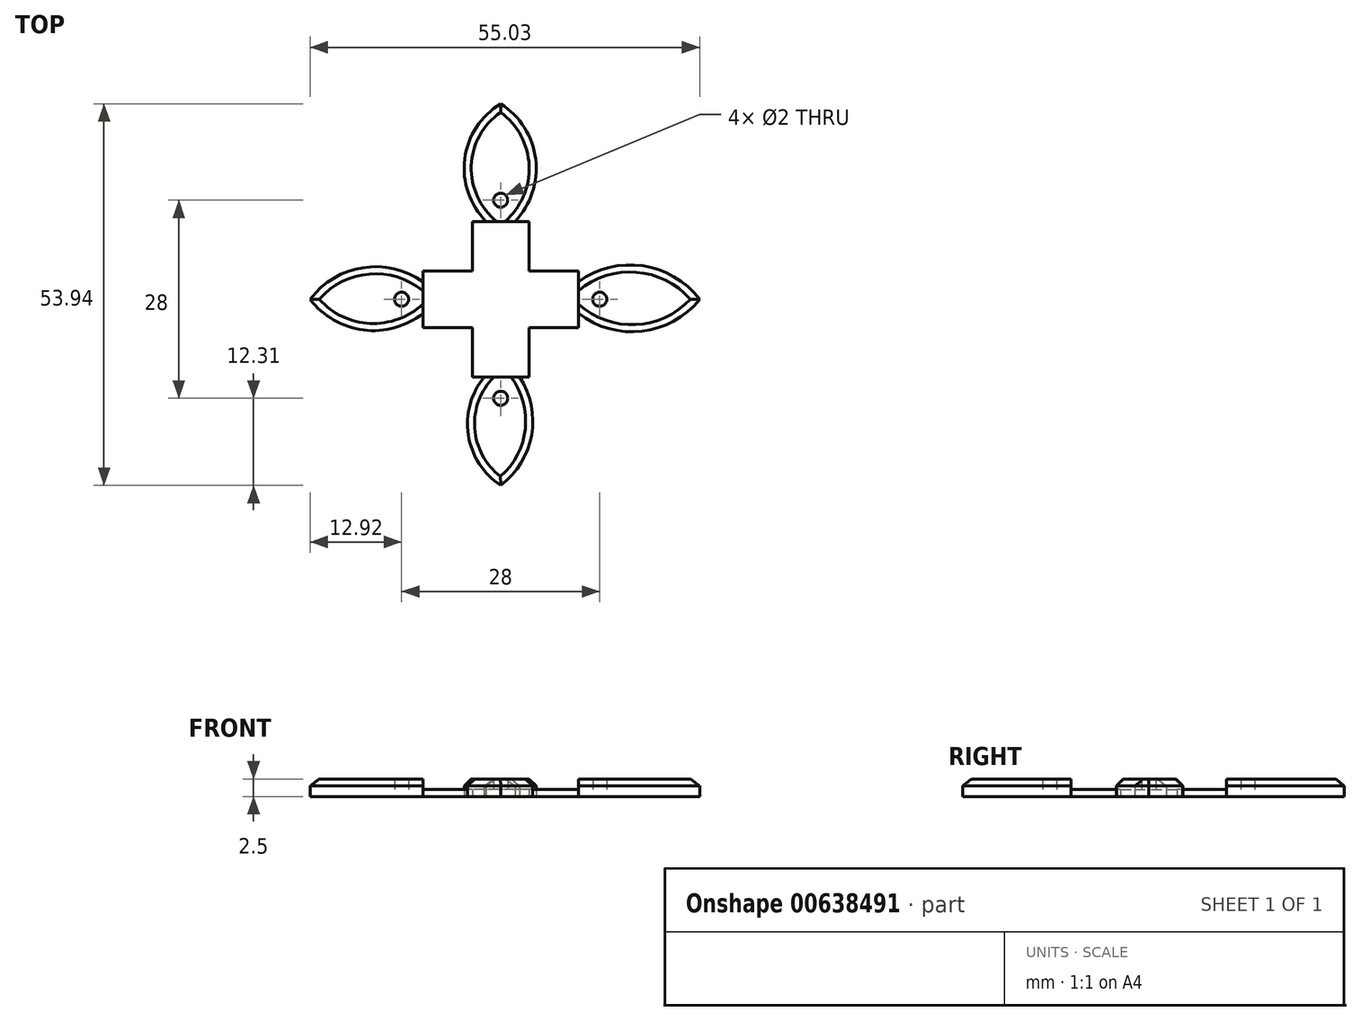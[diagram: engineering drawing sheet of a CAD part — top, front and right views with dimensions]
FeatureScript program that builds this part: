
annotation { "Feature Type Name" : "Feature", "Feature Type Description" : "" }
export const myFeature = defineFeature(function(context is Context, id is Id, definition is map)
    precondition{}
    {
        {
            var Q0;
            Q0=qCreatedBy(makeId("Top.planeOp"),FACE);
            var sketch = newSketch(context, id + "F0", { "sketchPlane" : qUnion([Q0])});
            skLineSegment(sketch, "E0.bottom", {"start": v(11, -4) * mm, "end": v(-11, -4) * mm});
            skLineSegment(sketch, "E0.top", {"start": v(11, 4) * mm, "end": v(-11, 4) * mm});
            skLineSegment(sketch, "E0.left", {"start": v(11, -4) * mm, "end": v(11, 4) * mm});
            skLineSegment(sketch, "E0.right", {"start": v(-11, -4) * mm, "end": v(-11, 4) * mm});
            skPoint(sketch, "E0.middle", {"position": v(0, 0) * mm});
            skLineSegment(sketch, "E1.bottom", {"start": v(4, 11) * mm, "end": v(-4, 11) * mm});
            skLineSegment(sketch, "E1.top", {"start": v(4, -11) * mm, "end": v(-4, -11) * mm});
            skLineSegment(sketch, "E1.left", {"start": v(4, 11) * mm, "end": v(4, -11) * mm});
            skLineSegment(sketch, "E1.right", {"start": v(-4, 11) * mm, "end": v(-4, -11) * mm});
            skSolve(sketch);
        }
        {
            var Q0;
            {var subQ0=sQuery(id+"F0.wireOp",EDGE,"E1.left");var subQ1=sQuery(id+"F0.wireOp",EDGE,"E0.bottom");var subQ2=makeQuery(id+"F0.imprint","INTERSECT",VERTEX,{"derivedFrom":[subQ1,subQ0]});Q0=makeQuery(id+"F0.imprint","IMPRINT",FACE,{"disambiguationData":[TD([[makeQuery(id+"F0.imprint","IMPRINT",EDGE,{"disambiguationData":[TD([[subQ2,-1.0]])],"derivedFrom":subQ1}),-1.0]])]});}
            var Q1;
            {var subQ0=sQuery(id+"F0.wireOp",EDGE,"E0.right");Q1=makeQuery(id+"F0.imprint","IMPRINT",FACE,{"disambiguationData":[TD([[makeQuery(id+"F0.imprint","IMPRINT",EDGE,{"derivedFrom":subQ0}),-1.0]])]});}
            var Q2;
            {var subQ5=sQuery(id+"F0.wireOp",EDGE,"E1.bottom");Q2=makeQuery(id+"F0.imprint","IMPRINT",FACE,{"disambiguationData":[TD([[makeQuery(id+"F0.imprint","IMPRINT",EDGE,{"derivedFrom":subQ5}),1.0]])]});}
            var Q3;
            {var subQ5=sQuery(id+"F0.wireOp",EDGE,"E1.top");Q3=makeQuery(id+"F0.imprint","IMPRINT",FACE,{"disambiguationData":[TD([[makeQuery(id+"F0.imprint","IMPRINT",EDGE,{"derivedFrom":subQ5}),-1.0]])]});}
            var Q4;
            {var subQ0=sQuery(id+"F0.wireOp",EDGE,"E0.left");Q4=makeQuery(id+"F0.imprint","IMPRINT",FACE,{"disambiguationData":[TD([[makeQuery(id+"F0.imprint","IMPRINT",EDGE,{"derivedFrom":subQ0}),1.0]])]});}
            extrude(context, id + "F1", {"entities" : qUnion([Q0, Q1, Q2, Q3, Q4]), "depth" : 1 * mm, "offsetDistance" : 25 * mm});
        }
        {
            var Q0;
            Q0=qCreatedBy(makeId("Top.planeOp"),FACE);
            var sketch = newSketch(context, id + "F2", { "sketchPlane" : qUnion([Q0])});
            skArc(sketch, "E2", {"start": v(0, 27.63) * mm, "mid": v(-5.08, 19.82) * mm, "end": v(-2.07, 11) * mm});
            skArc(sketch, "E3", {"start": v(2.04, 11) * mm, "mid": v(4.95, 19.8) * mm, "end": v(0, 27.63) * mm});
            skLineSegment(sketch, "E4", {"start": v(-2.07, 11) * mm, "end": v(2.04, 11) * mm});
            skArc(sketch, "E5", {"start": v(28.11, 0) * mm, "mid": v(20.06, 4.72) * mm, "end": v(11, 2.46) * mm});
            skArc(sketch, "E6", {"start": v(11, -1.99) * mm, "mid": v(19.97, -4.52) * mm, "end": v(28.11, 0) * mm});
            skArc(sketch, "E7", {"start": v(-2.32, -11) * mm, "mid": v(-4.57, -19.17) * mm, "end": v(0, -26.3) * mm});
            skArc(sketch, "E8", {"start": v(0, -26.3) * mm, "mid": v(4.36, -19.18) * mm, "end": v(2.68, -11) * mm});
            skArc(sketch, "E9", {"start": v(-11, 2.46) * mm, "mid": v(-19.46, 4.47) * mm, "end": v(-26.92, 0) * mm});
            skArc(sketch, "E10", {"start": v(-26.92, 0) * mm, "mid": v(-19.38, -4.34) * mm, "end": v(-11, -1.99) * mm});
            skLineSegment(sketch, "E11", {"start": v(11, 2.46) * mm, "end": v(11, -1.99) * mm});
            skLineSegment(sketch, "E12", {"start": v(2.68, -11) * mm, "end": v(-2.32, -11) * mm});
            skLineSegment(sketch, "E13", {"start": v(-11, -1.99) * mm, "end": v(-11, 2.46) * mm});
            skSolve(sketch);
        }
        {
            var Q0;
            Q0=makeQuery(id+"F2.imprint","IMPRINT",FACE,{"disambiguationData":[TD([[makeQuery(id+"F2.imprint","IMPRINT",EDGE,{"derivedFrom":sQuery(id+"F2.wireOp",EDGE,"E2")}),1.0]])]});
            var Q1;
            Q1=makeQuery(id+"F2.imprint","IMPRINT",FACE,{"disambiguationData":[TD([[makeQuery(id+"F2.imprint","IMPRINT",EDGE,{"derivedFrom":sQuery(id+"F2.wireOp",EDGE,"E9")}),1.0]])]});
            var Q2;
            Q2=makeQuery(id+"F2.imprint","IMPRINT",FACE,{"disambiguationData":[TD([[makeQuery(id+"F2.imprint","IMPRINT",EDGE,{"derivedFrom":sQuery(id+"F2.wireOp",EDGE,"E7")}),1.0]])]});
            var Q3;
            Q3=makeQuery(id+"F2.imprint","IMPRINT",FACE,{"disambiguationData":[TD([[makeQuery(id+"F2.imprint","IMPRINT",EDGE,{"derivedFrom":sQuery(id+"F2.wireOp",EDGE,"E5")}),1.0]])]});
            extrude(context, id + "F3", {"entities" : qUnion([Q0, Q1, Q2, Q3]), "operationType" : NewBodyOperationType.ADD, "depth" : 2.5 * mm, "offsetDistance" : 25 * mm});
        }
        {
            var Q0;
            Q0=makeQuery(id+"F3.boolean.opBoolean","MERGE",FACE,{"derivedFrom":[makeQuery(id+"F1.opExtrude","CAP_FACE",FACE,{"disambiguationData":[OSD([sQuery(id+"F0.wireOp",EDGE,"E0.bottom"),sQuery(id+"F0.wireOp",EDGE,"E0.top"),sQuery(id+"F0.wireOp",EDGE,"E0.left"),sQuery(id+"F0.wireOp",EDGE,"E0.right"),sQuery(id+"F0.wireOp",EDGE,"E1.bottom"),sQuery(id+"F0.wireOp",EDGE,"E1.top"),sQuery(id+"F0.wireOp",EDGE,"E1.left"),sQuery(id+"F0.wireOp",EDGE,"E1.right")])],"isStart":true}),makeQuery(id+"F3.opExtrude","CAP_FACE",FACE,{"disambiguationData":[OSD([sQuery(id+"F2.wireOp",EDGE,"E2"),sQuery(id+"F2.wireOp",EDGE,"E3"),sQuery(id+"F2.wireOp",EDGE,"E4")])],"isStart":true}),makeQuery(id+"F3.opExtrude","CAP_FACE",FACE,{"disambiguationData":[OSD([sQuery(id+"F2.wireOp",EDGE,"E5"),sQuery(id+"F2.wireOp",EDGE,"E6"),sQuery(id+"F2.wireOp",EDGE,"E11")])],"isStart":true}),makeQuery(id+"F3.opExtrude","CAP_FACE",FACE,{"disambiguationData":[OSD([sQuery(id+"F2.wireOp",EDGE,"E7"),sQuery(id+"F2.wireOp",EDGE,"E8"),sQuery(id+"F2.wireOp",EDGE,"E12")])],"isStart":true}),makeQuery(id+"F3.opExtrude","CAP_FACE",FACE,{"disambiguationData":[OSD([sQuery(id+"F2.wireOp",EDGE,"E9"),sQuery(id+"F2.wireOp",EDGE,"E10"),sQuery(id+"F2.wireOp",EDGE,"E13")])],"isStart":true})]});
            var sketch = newSketch(context, id + "F4", { "sketchPlane" : qUnion([Q0])});
            skCircle(sketch, "E14", {"center": v(0, 14) * mm, "radius": 1 * mm});
            skCircle(sketch, "E15", {"center": v(-14, 0) * mm, "radius": 1 * mm});
            skCircle(sketch, "E16", {"center": v(14, 0) * mm, "radius": 1 * mm});
            skCircle(sketch, "E17", {"center": v(0, -14) * mm, "radius": 1 * mm});
            skSolve(sketch);
        }
        {
            var Q0;
            Q0=makeQuery(id+"F4.imprint","IMPRINT",FACE,{"disambiguationData":[TD([[makeQuery(id+"F4.imprint","IMPRINT",EDGE,{"derivedFrom":sQuery(id+"F4.wireOp",EDGE,"E14")}),1.0]])]});
            var Q1;
            Q1=makeQuery(id+"F4.imprint","IMPRINT",FACE,{"disambiguationData":[TD([[makeQuery(id+"F4.imprint","IMPRINT",EDGE,{"derivedFrom":sQuery(id+"F4.wireOp",EDGE,"E15")}),1.0]])]});
            var Q2;
            Q2=makeQuery(id+"F4.imprint","IMPRINT",FACE,{"disambiguationData":[TD([[makeQuery(id+"F4.imprint","IMPRINT",EDGE,{"derivedFrom":sQuery(id+"F4.wireOp",EDGE,"E17")}),1.0]])]});
            var Q3;
            Q3=makeQuery(id+"F4.imprint","IMPRINT",FACE,{"disambiguationData":[TD([[makeQuery(id+"F4.imprint","IMPRINT",EDGE,{"derivedFrom":sQuery(id+"F4.wireOp",EDGE,"E16")}),1.0]])]});
            extrude(context, id + "F5", {"entities" : qUnion([Q0, Q1, Q2, Q3]), "operationType" : NewBodyOperationType.REMOVE, "endBound" : BoundingType.THROUGH_ALL, "oppositeDirection" : true, "depth" : 25 * mm, "offsetDistance" : 25 * mm});
        }
        {
            var Q0;
            Q0=makeQuery(id+"F3.opExtrude","CAP_EDGE",EDGE,{"disambiguationData":[OSD([sQuery(id+"F2.wireOp",EDGE,"E2")])],"isStart":false});
            var Q1;
            Q1=makeQuery(id+"F3.opExtrude","CAP_EDGE",EDGE,{"disambiguationData":[OSD([sQuery(id+"F2.wireOp",EDGE,"E3")])],"isStart":false});
            var Q2;
            Q2=makeQuery(id+"F3.opExtrude","CAP_EDGE",EDGE,{"disambiguationData":[OSD([sQuery(id+"F2.wireOp",EDGE,"E5")])],"isStart":false});
            var Q3;
            Q3=makeQuery(id+"F3.opExtrude","CAP_EDGE",EDGE,{"disambiguationData":[OSD([sQuery(id+"F2.wireOp",EDGE,"E8")])],"isStart":false});
            var Q4;
            Q4=makeQuery(id+"F3.opExtrude","CAP_EDGE",EDGE,{"disambiguationData":[OSD([sQuery(id+"F2.wireOp",EDGE,"E6")])],"isStart":false});
            var Q5;
            Q5=makeQuery(id+"F3.opExtrude","CAP_EDGE",EDGE,{"disambiguationData":[OSD([sQuery(id+"F2.wireOp",EDGE,"E7")])],"isStart":false});
            var Q6;
            Q6=makeQuery(id+"F3.opExtrude","CAP_EDGE",EDGE,{"disambiguationData":[OSD([sQuery(id+"F2.wireOp",EDGE,"E9")])],"isStart":false});
            var Q7;
            Q7=makeQuery(id+"F3.opExtrude","CAP_EDGE",EDGE,{"disambiguationData":[OSD([sQuery(id+"F2.wireOp",EDGE,"E10")])],"isStart":false});
            chamfer(context, id + "F6", {"entities" : qUnion([Q0, Q1, Q2, Q3, Q4, Q5, Q6, Q7]), "width" : 1 * mm, "tangentPropagation" : true});
        }
    });
